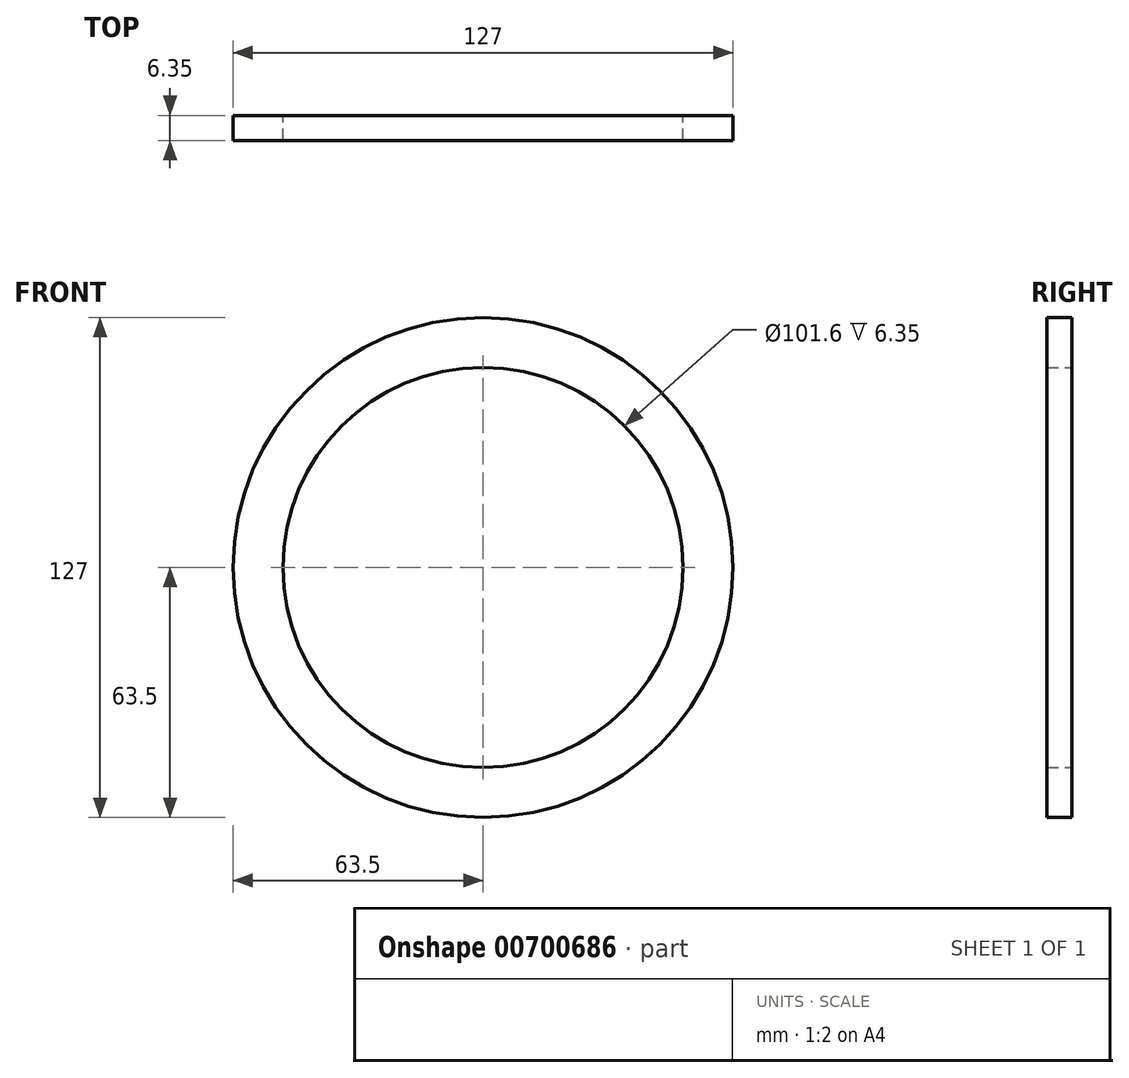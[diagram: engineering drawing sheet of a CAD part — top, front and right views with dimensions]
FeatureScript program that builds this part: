
annotation { "Feature Type Name" : "Feature", "Feature Type Description" : "" }
export const myFeature = defineFeature(function(context is Context, id is Id, definition is map)
    precondition{}
    {
        {
            var Q0;
            Q0=qCreatedBy(makeId("Front.planeOp"),FACE);
            var sketch = newSketch(context, id + "F0", { "sketchPlane" : qUnion([Q0])});
            skCircle(sketch, "E0", {"center": v(0, 0) * mm, "radius": 63.5 * mm});
            skCircle(sketch, "E1", {"center": v(0, 0) * mm, "radius": 50.8 * mm});
            skSolve(sketch);
        }
        {
            var Q0;
            Q0=makeQuery(id+"F0.imprint","IMPRINT",FACE,{"disambiguationData":[TD([[makeQuery(id+"F0.imprint","IMPRINT",EDGE,{"derivedFrom":sQuery(id+"F0.wireOp",EDGE,"E0")}),1.0]])]});
            extrude(context, id + "F1", {"entities" : qUnion([Q0]), "depth" : 6.35 * mm, "offsetDistance" : 25.4 * mm});
        }
    });
